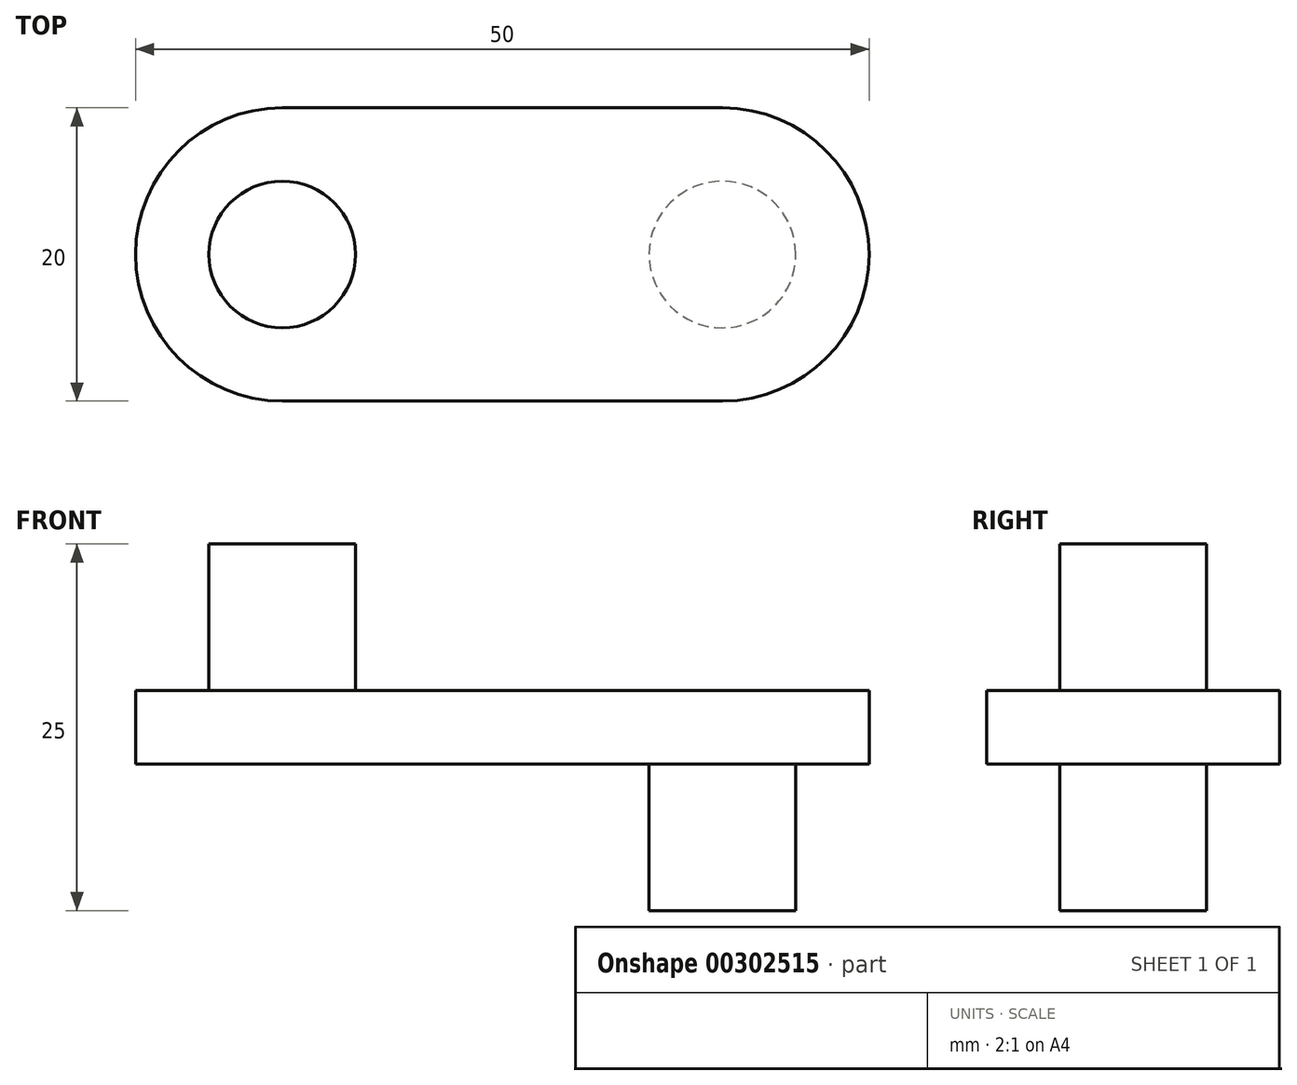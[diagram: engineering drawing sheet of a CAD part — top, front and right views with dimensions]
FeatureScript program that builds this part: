
annotation { "Feature Type Name" : "Feature", "Feature Type Description" : "" }
export const myFeature = defineFeature(function(context is Context, id is Id, definition is map)
    precondition{}
    {
        {
            var Q0;
            Q0=qCreatedBy(makeId("Top.planeOp"),FACE);
            var sketch = newSketch(context, id + "F0", { "sketchPlane" : qUnion([Q0])});
            skLineSegment(sketch, "E0.bottom", {"start": v(0, 0) * mm, "end": v(30, 0) * mm});
            skLineSegment(sketch, "E0.top", {"start": v(0, 20) * mm, "end": v(30, 20) * mm});
            skLineSegment(sketch, "E0.left", {"start": v(0, 0) * mm, "end": v(0, 20) * mm});
            skLineSegment(sketch, "E0.right", {"start": v(30, 0) * mm, "end": v(30, 20) * mm});
            skArc(sketch, "E1", {"start": v(30, 0) * mm, "mid": v(40, 10) * mm, "end": v(30, 20) * mm});
            skArc(sketch, "E2", {"start": v(0, 20) * mm, "mid": v(-10, 10) * mm, "end": v(0, 0) * mm});
            skSolve(sketch);
        }
        {
            var Q0;
            Q0 = qSketchRegion(id + "F0", true);
            extrude(context, id + "F1", {"entities" : qUnion([Q0]), "depth" : 5 * mm});
        }
        {
            var Q0;
            Q0=makeQuery(id+"F1.opExtrude","CAP_FACE",FACE,{"disambiguationData":[OSD([sQuery(id+"F0.wireOp",EDGE,"E0.bottom"),sQuery(id+"F0.wireOp",EDGE,"E0.top"),sQuery(id+"F0.wireOp",EDGE,"E1"),sQuery(id+"F0.wireOp",EDGE,"E2")])],"isStart":false});
            var sketch = newSketch(context, id + "F2", { "sketchPlane" : qUnion([Q0])});
            skCircle(sketch, "E3", {"center": v(0, 10) * mm, "radius": 5 * mm});
            skSolve(sketch);
        }
        {
            var Q0;
            Q0 = qSketchRegion(id + "F2", true);
            extrude(context, id + "F3", {"entities" : qUnion([Q0]), "operationType" : NewBodyOperationType.ADD, "depth" : 10 * mm});
        }
        {
            var Q0;
            Q0=makeQuery(id+"F1.opExtrude","CAP_FACE",FACE,{"disambiguationData":[OSD([sQuery(id+"F0.wireOp",EDGE,"E0.bottom"),sQuery(id+"F0.wireOp",EDGE,"E0.top"),sQuery(id+"F0.wireOp",EDGE,"E1"),sQuery(id+"F0.wireOp",EDGE,"E2")])],"isStart":false});
            var sketch = newSketch(context, id + "F4", { "sketchPlane" : qUnion([Q0])});
            skCircle(sketch, "E4", {"center": v(30, 10) * mm, "radius": 5 * mm});
            skSolve(sketch);
        }
        {
            var Q0;
            Q0 = qSketchRegion(id + "F4", true);
            extrude(context, id + "F5", {"entities" : qUnion([Q0]), "operationType" : NewBodyOperationType.ADD, "oppositeDirection" : true, "depth" : 15 * mm});
        }
    });
